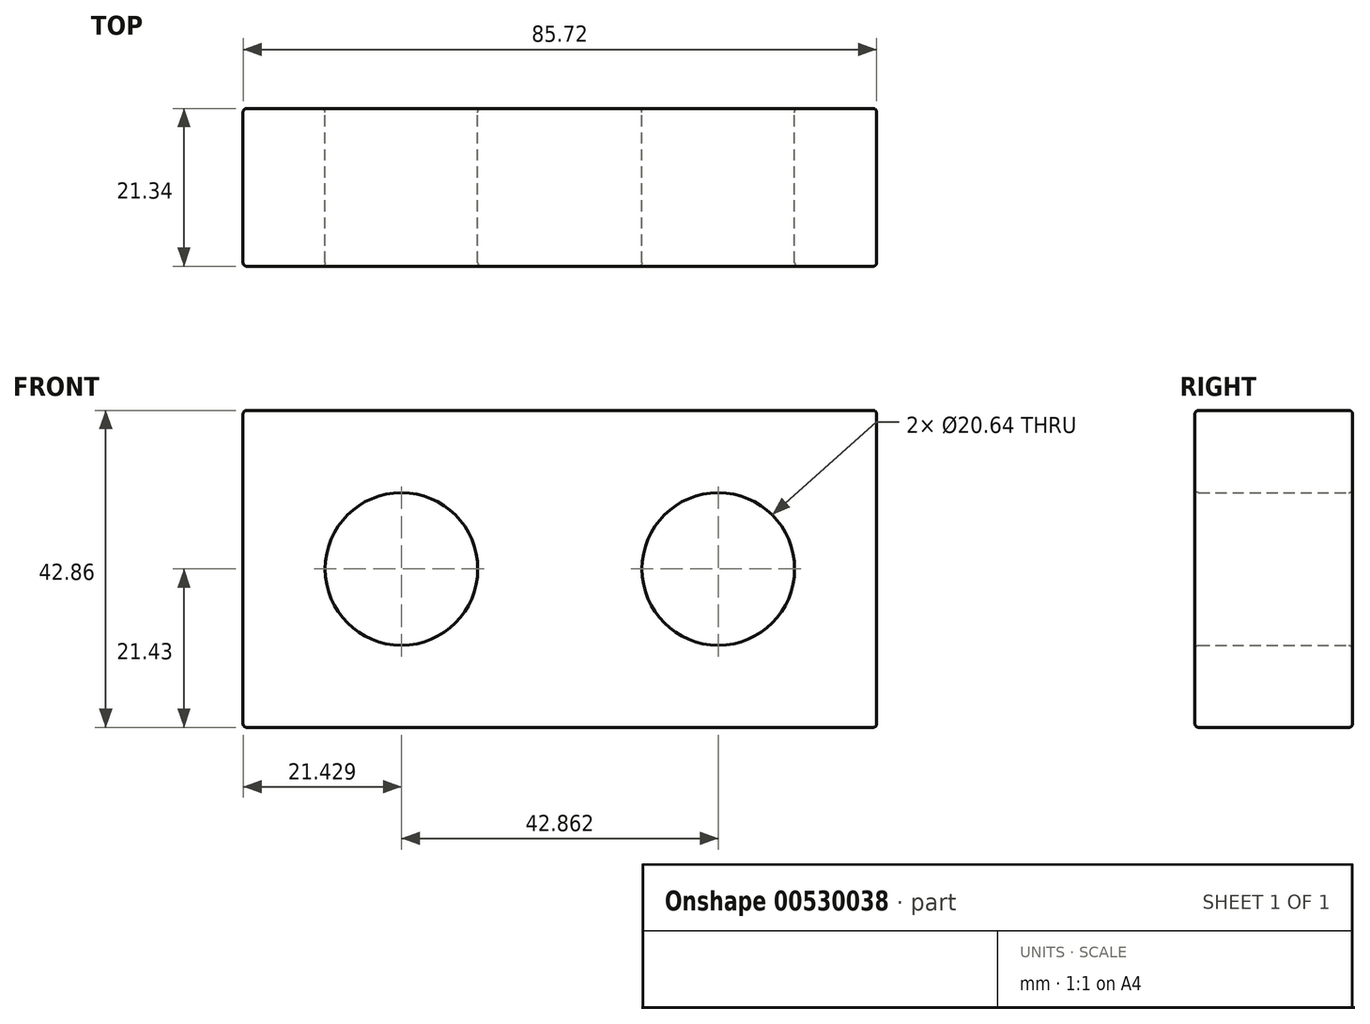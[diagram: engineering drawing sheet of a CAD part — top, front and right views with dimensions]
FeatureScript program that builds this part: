
annotation { "Feature Type Name" : "Feature", "Feature Type Description" : "" }
export const myFeature = defineFeature(function(context is Context, id is Id, definition is map)
    precondition{}
    {
        {
            var Q0;
            Q0=qCreatedBy(makeId("Front.planeOp"),FACE);
            var sketch = newSketch(context, id + "F0", { "sketchPlane" : qUnion([Q0])});
            skLineSegment(sketch, "E0.bottom", {"start": v(42.86, 21.43) * mm, "end": v(-42.86, 21.43) * mm});
            skLineSegment(sketch, "E0.top", {"start": v(42.86, -21.43) * mm, "end": v(-42.86, -21.43) * mm});
            skLineSegment(sketch, "E0.left", {"start": v(42.86, 21.43) * mm, "end": v(42.86, -21.43) * mm});
            skLineSegment(sketch, "E0.right", {"start": v(-42.86, 21.43) * mm, "end": v(-42.86, -21.43) * mm});
            skPoint(sketch, "E0.middle", {"position": v(0, 0) * mm});
            skLineSegment(sketch, "E1", {"start": v(-42.86, 0) * mm, "end": v(0, 0) * mm, "construction": true});
            skLineSegment(sketch, "E2", {"start": v(0, 0) * mm, "end": v(42.86, 0) * mm, "construction": true});
            skCircle(sketch, "E3", {"center": v(-21.43, 0) * mm, "radius": 10.32 * mm});
            skCircle(sketch, "E4", {"center": v(21.43, 0) * mm, "radius": 10.32 * mm});
            skSolve(sketch);
        }
        {
            var Q0;
            Q0=qSketchRegion(id+"F0",true);
            extrude(context, id + "F1", {"entities" : qUnion([Q0]), "depth" : 21.34 * mm});
        }
        {
            var Q0;
            Q0=makeQuery(id+"F1.opExtrude","CAP_EDGE",EDGE,{"disambiguationData":[OSD([sQuery(id+"F0.wireOp",EDGE,"E0.bottom")])],"isStart":false});
            var Q1;
            Q1=makeQuery(id+"F1.opExtrude","CAP_EDGE",EDGE,{"disambiguationData":[OSD([sQuery(id+"F0.wireOp",EDGE,"E0.bottom")])],"isStart":true});
            var Q2;
            Q2=makeQuery(id+"F1.opExtrude","SWEPT_EDGE",EDGE,{"disambiguationData":[OSD([sQuery(id+"F0.wireOp",EDGE,"E0.bottom"),sQuery(id+"F0.wireOp",EDGE,"E0.right")])]});
            var Q3;
            Q3=makeQuery(id+"F1.opExtrude","SWEPT_EDGE",EDGE,{"disambiguationData":[OSD([sQuery(id+"F0.wireOp",EDGE,"E0.bottom"),sQuery(id+"F0.wireOp",EDGE,"E0.left")])]});
            var Q4;
            Q4=makeQuery(id+"F1.opExtrude","CAP_EDGE",EDGE,{"disambiguationData":[OSD([sQuery(id+"F0.wireOp",EDGE,"E0.left")])],"isStart":false});
            var Q5;
            Q5=makeQuery(id+"F1.opExtrude","CAP_EDGE",EDGE,{"disambiguationData":[OSD([sQuery(id+"F0.wireOp",EDGE,"E0.left")])],"isStart":true});
            var Q6;
            Q6=makeQuery(id+"F1.opExtrude","SWEPT_EDGE",EDGE,{"disambiguationData":[OSD([sQuery(id+"F0.wireOp",EDGE,"E0.top"),sQuery(id+"F0.wireOp",EDGE,"E0.left")])]});
            var Q7;
            Q7=makeQuery(id+"F1.opExtrude","CAP_EDGE",EDGE,{"disambiguationData":[OSD([sQuery(id+"F0.wireOp",EDGE,"E0.top")])],"isStart":false});
            var Q8;
            Q8=makeQuery(id+"F1.opExtrude","CAP_EDGE",EDGE,{"disambiguationData":[OSD([sQuery(id+"F0.wireOp",EDGE,"E0.right")])],"isStart":false});
            var Q9;
            Q9=makeQuery(id+"F1.opExtrude","CAP_EDGE",EDGE,{"disambiguationData":[OSD([sQuery(id+"F0.wireOp",EDGE,"E4")])],"isStart":false});
            var Q10;
            Q10=makeQuery(id+"F1.opExtrude","CAP_EDGE",EDGE,{"disambiguationData":[OSD([sQuery(id+"F0.wireOp",EDGE,"E3")])],"isStart":false});
            var Q11;
            Q11=makeQuery(id+"F1.opExtrude","SWEPT_EDGE",EDGE,{"disambiguationData":[OSD([sQuery(id+"F0.wireOp",EDGE,"E0.top"),sQuery(id+"F0.wireOp",EDGE,"E0.right")])]});
            var Q12;
            Q12=makeQuery(id+"F1.opExtrude","CAP_EDGE",EDGE,{"disambiguationData":[OSD([sQuery(id+"F0.wireOp",EDGE,"E0.right")])],"isStart":true});
            var Q13;
            Q13=makeQuery(id+"F1.opExtrude","CAP_EDGE",EDGE,{"disambiguationData":[OSD([sQuery(id+"F0.wireOp",EDGE,"E0.top")])],"isStart":true});
            var Q14;
            Q14=makeQuery(id+"F1.opExtrude","CAP_EDGE",EDGE,{"disambiguationData":[OSD([sQuery(id+"F0.wireOp",EDGE,"E3")])],"isStart":true});
            var Q15;
            Q15=makeQuery(id+"F1.opExtrude","CAP_EDGE",EDGE,{"disambiguationData":[OSD([sQuery(id+"F0.wireOp",EDGE,"E4")])],"isStart":true});
            fillet(context, id + "F2", {"entities" : qUnion([Q0, Q1, Q2, Q3, Q4, Q5, Q6, Q7, Q8, Q9, Q10, Q11, Q12, Q13, Q14, Q15]), "radius" : 0.5 * mm, "tangentPropagation" : true, "allowEdgeOverflow" : false});
        }
    });
